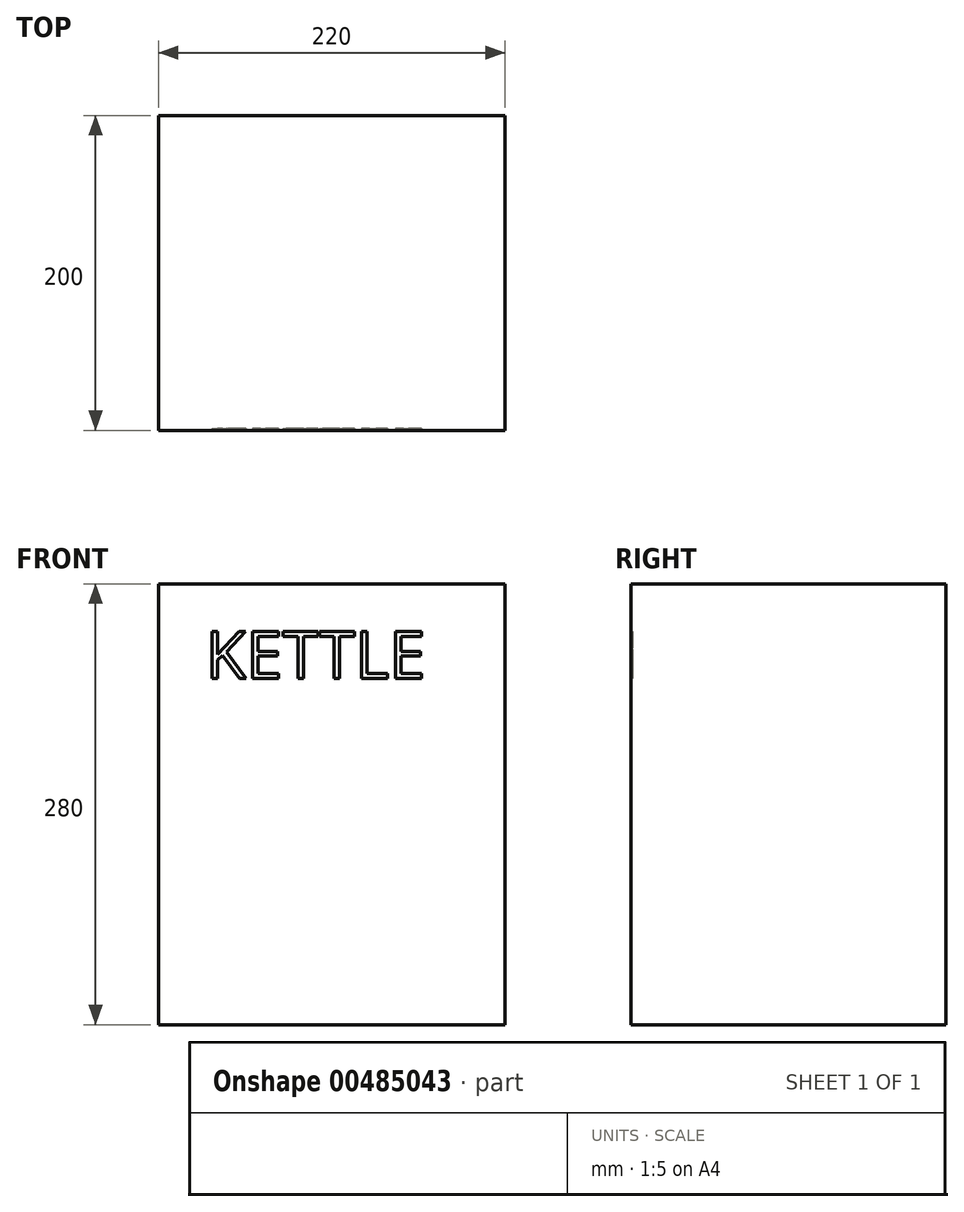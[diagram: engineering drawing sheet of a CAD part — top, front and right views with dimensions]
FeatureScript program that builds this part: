
annotation { "Feature Type Name" : "Feature", "Feature Type Description" : "" }
export const myFeature = defineFeature(function(context is Context, id is Id, definition is map)
    precondition{}
    {
        {
            var Q0;
            Q0=qCreatedBy(makeId("Top.planeOp"),FACE);
            var sketch = newSketch(context, id + "F0", { "sketchPlane" : qUnion([Q0])});
            skLineSegment(sketch, "E0.bottom", {"start": v(110, -100) * mm, "end": v(-110, -100) * mm});
            skLineSegment(sketch, "E0.top", {"start": v(110, 100) * mm, "end": v(-110, 100) * mm});
            skLineSegment(sketch, "E0.left", {"start": v(110, -100) * mm, "end": v(110, 100) * mm});
            skLineSegment(sketch, "E0.right", {"start": v(-110, -100) * mm, "end": v(-110, 100) * mm});
            skPoint(sketch, "E0.middle", {"position": v(0, 0) * mm});
            skSolve(sketch);
        }
        {
            var Q0;
            Q0=makeQuery(id+"F0.imprint","IMPRINT",FACE,{"disambiguationData":[TD([[makeQuery(id+"F0.imprint","IMPRINT",EDGE,{"derivedFrom":sQuery(id+"F0.wireOp",EDGE,"E0.bottom")}),-1.0]])]});
            extrude(context, id + "F1", {"entities" : qUnion([Q0]), "depth" : 280 * mm});
        }
        {
            var Q0;
            Q0=makeQuery(id+"F1.opExtrude","SWEPT_FACE",FACE,{"disambiguationData":[OSD([sQuery(id+"F0.wireOp",EDGE,"E0.bottom")])]});
            var sketch = newSketch(context, id + "F2", { "sketchPlane" : qUnion([Q0])});
            skText(sketch, "E1", { "text": "KETTLE", "fontName": "OpenSans-Regular.ttf"});
            const initialGuessF2  = {"E1": [-0.08, 0.22, 1, 0, 0.03]};
            skSetInitialGuess(sketch, initialGuessF2);
            skSolve(sketch);
        }
        {
            var Q0;
            Q0 = qSketchRegion(id + "F2", true);
            extrude(context, id + "F3", {"entities" : qUnion([Q0]), "operationType" : NewBodyOperationType.REMOVE, "oppositeDirection" : true, "depth" : 1 * mm});
        }
    });
